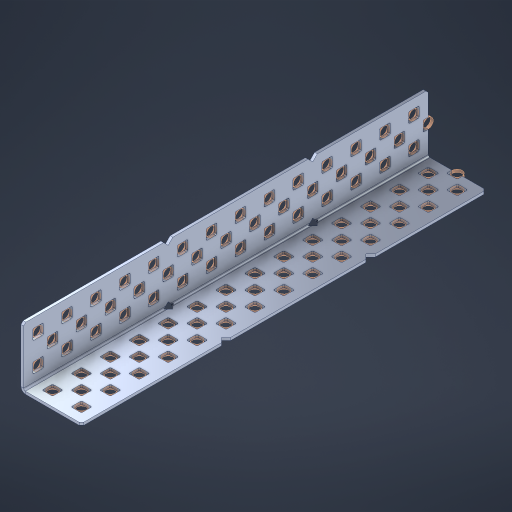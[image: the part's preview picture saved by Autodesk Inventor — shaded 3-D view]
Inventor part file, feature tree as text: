
AUTODESK INVENTOR PART (.ipt)
format: ipt  version: 2023 (Build 270158000, 158)  size: 1,184,768 bytes
history: native  units: in
note: dims shown in document units (in); Inventor stores cm internally (conversion verified against a paired STEP export)
features: other x90, extrude x82, sheet_metal_op x8, sketch x7, pattern_linear x2, mirror x1, chamfer x1
ambient origin geometry x8: Origin, YZ Plane, XZ Plane, XY Plane, X Axis, Y Axis, Z Axis, Center Point
bodies: Solid1 (feature_tree), Body (feature_tree)
feature tree (191):
  sheet_metal_op  "Flanges"
  sheet_metal_op  "Body Pattern"
  pattern_linear  "Center Pattern"  Spacing1=1.0in  [1 undecoded]
  other  "Arc Length"
  pattern_linear  "Notch Pattern"  Spacing1=0.1875in  [1 undecoded]
  other  "Diagonal Plane"
  mirror  "Everything Mirrored"
  chamfer  "End Chamfer"
  sketch  "Sketch1"  dims[d0=1.0in]
  other  "Plate1"
  sketch  "Sketch2"  dims[d1=7.0in]
  other  "Plate2"
  sheet_metal_op  "Bend1"
  sheet_metal_op  "Corner1"
  sketch  "Sketch8"  dims[d2=0.0469in]
  sketch  "Sketch9"  dims[d3=0.0469in]
  other  "Srf91"
  sheet_metal_op  "Body Pattern Sketch"
  other  "Srf92"
  sketch  "Sketch13"  dims[d4=0.0234in]
  sketch  "Sketch15"  dims[d5=0.0938in]
  sketch  "Sketch16"  dims[d6=0.0469in d7=1.0in d8=90.0deg d9=0.0312in d10=0.1875in d11=0.0469in d12=0.0469in d49=0.182in d50=0.02in d52=0.25in d53=0.0469in d54=0.0in d55=0.172in d56=1.0in d57=0.0in d60=5.5118in d62=0.5in d63=0.7874in d65=0.5in d85=0.1473in d86=0.1659in d89=0.0469in d90=0.0in d91=0.04in d92=0.0491in d95=2.5in d96=0.04in d97=0.25in d98=45.0deg d99=0.25in d106=0.182in d107=0.02in d108=0.5in d110=0.0469in d111=0.0in d112=0.172in d113=0.5in d114=0.0in d117=0.5in d123=0.25in d125=0.25in d126=0.0491in d127=0.1227in d128=0.08in d129=0.04in d130=2.5in]
  other  "Srf786"
  other  "Srf856"
  other  "Srf857"
  other  "Srf858"
  other  "Srf859"
  other  "Srf860"
  other  "Srf861"
  other  "Srf889"
  other  "Srf890"
  other  "Srf891"
  other  "Srf1275"
  other  "Srf1276"
  other  "Srf1278"
  other  "Srf1279"
  other  "Srf1280"
  other  "Srf1281"
  other  "Srf1282"
  other  "Srf1283"
  other  "Srf1277"
  other  "Srf1285"
  other  "Srf1286"
  other  "Srf1287"
  other  "Srf1383"
  other  "Srf1384"
  other  "Srf1385"
  other  "Srf1386"
  other  "Srf1387"
  other  "Srf1388"
  other  "Srf1389"
  other  "Srf1390"
  other  "Srf1391"
  other  "Srf1392"
  other  "Srf1393"
  other  "Srf1394"
  other  "Srf1395"
  other  "Srf1396"
  other  "Srf1397"
  other  "Srf1398"
  other  "Srf1399"
  other  "Srf1400"
  other  "Srf1401"
  other  "Srf1402"
  other  "Srf1445"
  other  "Srf1446"
  other  "Srf1447"
  other  "Srf1448"
  other  "Srf1449"
  other  "Srf1450"
  other  "Srf1451"
  other  "Srf1452"
  other  "Srf1453"
  other  "Srf1454"
  other  "Srf1475"
  other  "Srf1476"
  other  "Srf1477"
  other  "Srf1478"
  other  "Srf1479"
  other  "Srf1480"
  other  "Srf1481"
  other  "Srf1482"
  other  "Srf1483"
  other  "Srf1484"
  other  "Srf1485"
  other  "Srf1486"
  other  "Srf1487"
  other  "Srf1488"
  other  "Srf1489"
  other  "Srf1490"
  other  "Srf1491"
  other  "Srf1492"
  other  "Srf1493"
  other  "Srf1494"
  other  "Srf1537"
  other  "Srf1538"
  other  "Srf1539"
  other  "Srf1540"
  other  "Srf1541"
  other  "Srf1542"
  other  "Srf1543"
  other  "Srf1544"
  other  "Srf1545"
  other  "Srf1546"
  sheet_metal_op  "Body Stamp"
  sheet_metal_op  "Body Circle"
  other  "Center Stamp"
  other  "Center Circle"
  sheet_metal_op  "Notch"
  extrude  "ExtrusionSrf92"  Depth=0.0469in
  extrude  "ExtrusionSrf856"  Depth=0.0469in
  extrude  "ExtrusionSrf857"  Depth=0.182in
  extrude  "ExtrusionSrf858"  Depth=0.02in
  extrude  "ExtrusionSrf859"  Depth=0.25in
  extrude  "ExtrusionSrf860"  Depth=0.0469in
  extrude  "ExtrusionSrf861"  TaperAngle=0.0deg  [1 undecoded]
  extrude  "ExtrusionSrf889"  Depth=2.5in
  extrude  "ExtrusionSrf890"  Depth=1.0in TaperAngle=0.0deg
  extrude  "ExtrusionSrf891"  Depth=2.5in
  extrude  "ExtrusionSrf1275"  Depth=0.5in
  extrude  "ExtrusionSrf1276"  Depth=2.5in
  extrude  "ExtrusionSrf1277"  Depth=2.5in
  extrude  "ExtrusionSrf1278"  Depth=0.0469in
  extrude  "ExtrusionSrf1279"  Depth=2.5in TaperAngle=0.0deg
  extrude  "ExtrusionSrf1280"  Depth=2.5in
  extrude  "ExtrusionSrf1281"  Depth=0.25in TaperAngle=45.0deg
  extrude  "ExtrusionSrf1282"  Depth=0.25in
  extrude  "ExtrusionSrf1345"  Depth=0.182in
  extrude  "ExtrusionSrf1346"  Depth=0.02in
  extrude  "ExtrusionSrf1347"  Depth=0.5in
  extrude  "ExtrusionSrf1348"  Depth=0.0469in
  extrude  "ExtrusionSrf1383"  TaperAngle=0.0deg  [1 undecoded]
  extrude  "ExtrusionSrf1384"  Depth=2.5in
  extrude  "ExtrusionSrf1385"  Depth=0.5in TaperAngle=0.0deg
  extrude  "ExtrusionSrf1386"  Depth=0.5in
  extrude  "ExtrusionSrf1387"  Depth=0.25in
  extrude  "ExtrusionSrf1388"  Depth=0.25in
  extrude  "ExtrusionSrf1389"  Depth=2.5in
  extrude  "ExtrusionSrf1390"  Depth=2.5in
  extrude  "ExtrusionSrf1391"  Depth=2.5in
  extrude  "ExtrusionSrf1392"  Depth=2.5in
  extrude  "ExtrusionSrf1393"  Depth=2.5in
  extrude  "ExtrusionSrf1394"  [1 undecoded]
  extrude  "ExtrusionSrf1395"  [1 undecoded]
  extrude  "ExtrusionSrf1396"  [1 undecoded]
  extrude  "ExtrusionSrf1397"  [1 undecoded]
  extrude  "ExtrusionSrf1398"  [1 undecoded]
  extrude  "ExtrusionSrf1399"  [1 undecoded]
  extrude  "ExtrusionSrf1400"  [1 undecoded]
  extrude  "ExtrusionSrf1401"  [1 undecoded]
  extrude  "ExtrusionSrf1402"  [1 undecoded]
  extrude  "ExtrusionSrf1445"  [1 undecoded]
  extrude  "ExtrusionSrf1446"  [1 undecoded]
  extrude  "ExtrusionSrf1447"  [1 undecoded]
  extrude  "ExtrusionSrf1448"  [1 undecoded]
  extrude  "ExtrusionSrf1449"  [1 undecoded]
  extrude  "ExtrusionSrf1450"  [1 undecoded]
  extrude  "ExtrusionSrf1451"  [1 undecoded]
  extrude  "ExtrusionSrf1452"  [1 undecoded]
  extrude  "ExtrusionSrf1453"  [1 undecoded]
  extrude  "ExtrusionSrf1454"  [1 undecoded]
  extrude  "ExtrusionSrf1475"  [1 undecoded]
  extrude  "ExtrusionSrf1476"  [1 undecoded]
  extrude  "ExtrusionSrf1477"  [1 undecoded]
  extrude  "ExtrusionSrf1478"  [1 undecoded]
  extrude  "ExtrusionSrf1479"  [1 undecoded]
  extrude  "ExtrusionSrf1480"  [1 undecoded]
  extrude  "ExtrusionSrf1481"  [1 undecoded]
  extrude  "ExtrusionSrf1482"  [1 undecoded]
  extrude  "ExtrusionSrf1483"  [1 undecoded]
  extrude  "ExtrusionSrf1484"  [1 undecoded]
  extrude  "ExtrusionSrf1485"  [1 undecoded]
  extrude  "ExtrusionSrf1486"  [1 undecoded]
  extrude  "ExtrusionSrf1487"  [1 undecoded]
  extrude  "ExtrusionSrf1488"  [1 undecoded]
  extrude  "ExtrusionSrf1489"  [1 undecoded]
  extrude  "ExtrusionSrf1490"  [1 undecoded]
  extrude  "ExtrusionSrf1491"  [1 undecoded]
  extrude  "ExtrusionSrf1492"  [1 undecoded]
  extrude  "ExtrusionSrf1493"  [1 undecoded]
  extrude  "ExtrusionSrf1494"  [1 undecoded]
  extrude  "ExtrusionSrf1537"  [1 undecoded]
  extrude  "ExtrusionSrf1538"  [1 undecoded]
  extrude  "ExtrusionSrf1539"  [1 undecoded]
  extrude  "ExtrusionSrf1540"  [1 undecoded]
  extrude  "ExtrusionSrf1541"  [1 undecoded]
  extrude  "ExtrusionSrf1542"  [1 undecoded]
  extrude  "ExtrusionSrf1543"  [1 undecoded]
  extrude  "ExtrusionSrf1544"  [1 undecoded]
  extrude  "ExtrusionSrf1545"  [1 undecoded]
  extrude  "ExtrusionSrf1546"  [1 undecoded]
note: 53 required parameter values undecoded (feature->parameter linkage not recoverable at this tier; creation-order binding heuristic only, values carry confidence <= 0.55)
